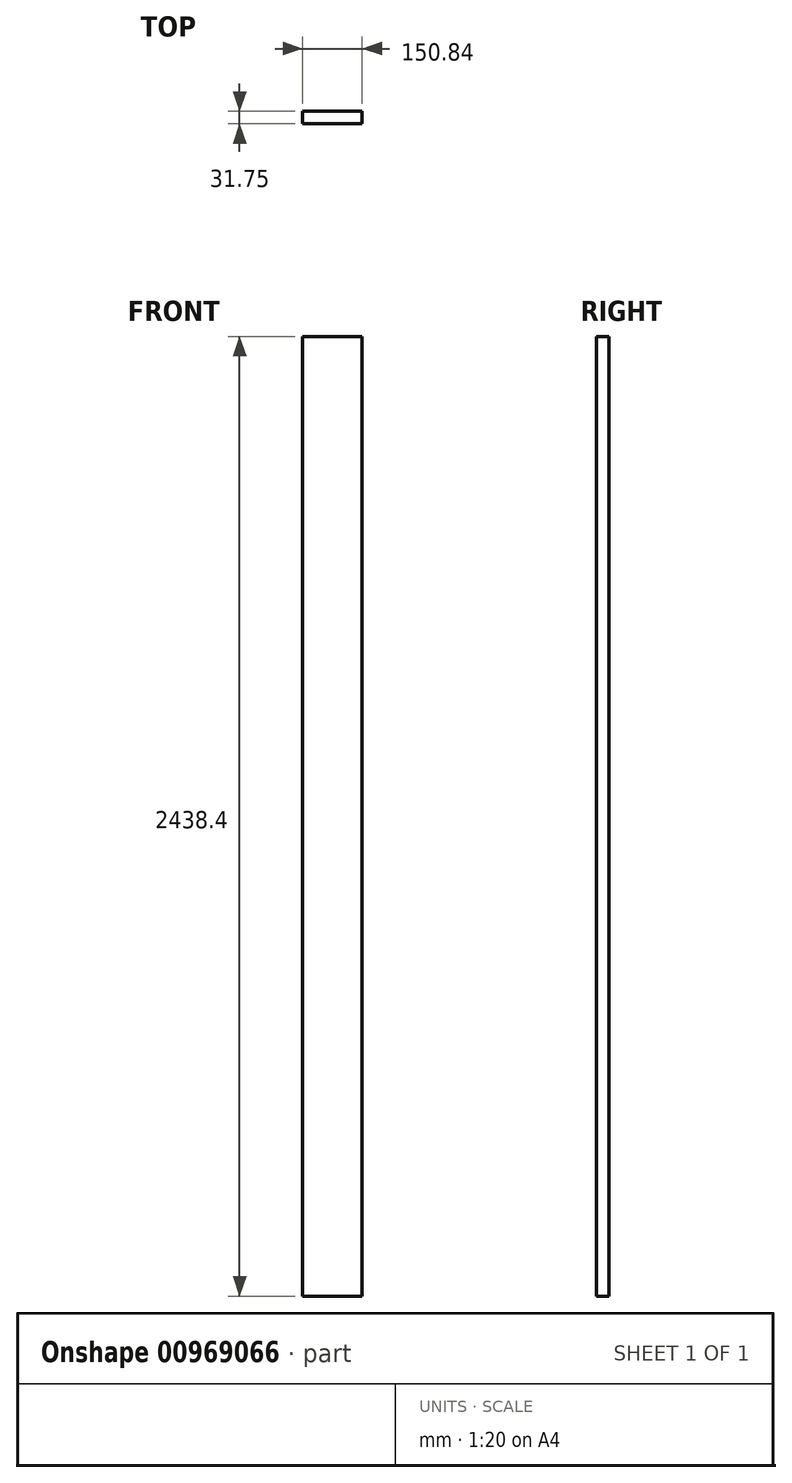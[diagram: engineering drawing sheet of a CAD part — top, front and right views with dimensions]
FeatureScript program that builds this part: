
annotation { "Feature Type Name" : "Feature", "Feature Type Description" : "" }
export const myFeature = defineFeature(function(context is Context, id is Id, definition is map)
    precondition{}
    {
        {
            var Q0;
            Q0=qCreatedBy(makeId("Top.planeOp"),FACE);
            var sketch = newSketch(context, id + "F0", { "sketchPlane" : qUnion([Q0])});
            skLineSegment(sketch, "E0.bottom", {"start": v(0, 0) * mm, "end": v(150.84, 0) * mm});
            skLineSegment(sketch, "E0.top", {"start": v(0, -31.75) * mm, "end": v(150.84, -31.75) * mm});
            skLineSegment(sketch, "E0.left", {"start": v(0, 0) * mm, "end": v(0, -31.75) * mm});
            skLineSegment(sketch, "E0.right", {"start": v(150.84, 0) * mm, "end": v(150.84, -31.75) * mm});
            skSolve(sketch);
        }
        {
            var Q0;
            Q0=makeQuery(id+"F0.imprint","IMPRINT",FACE,{"disambiguationData":[TD([[makeQuery(id+"F0.imprint","IMPRINT",EDGE,{"derivedFrom":sQuery(id+"F0.wireOp",EDGE,"E0.bottom")}),-1.0]])]});
            extrude(context, id + "F1", {"entities" : qUnion([Q0]), "depth" : 2438.4 * mm, "offsetDistance" : 25.4 * mm});
        }
    });
